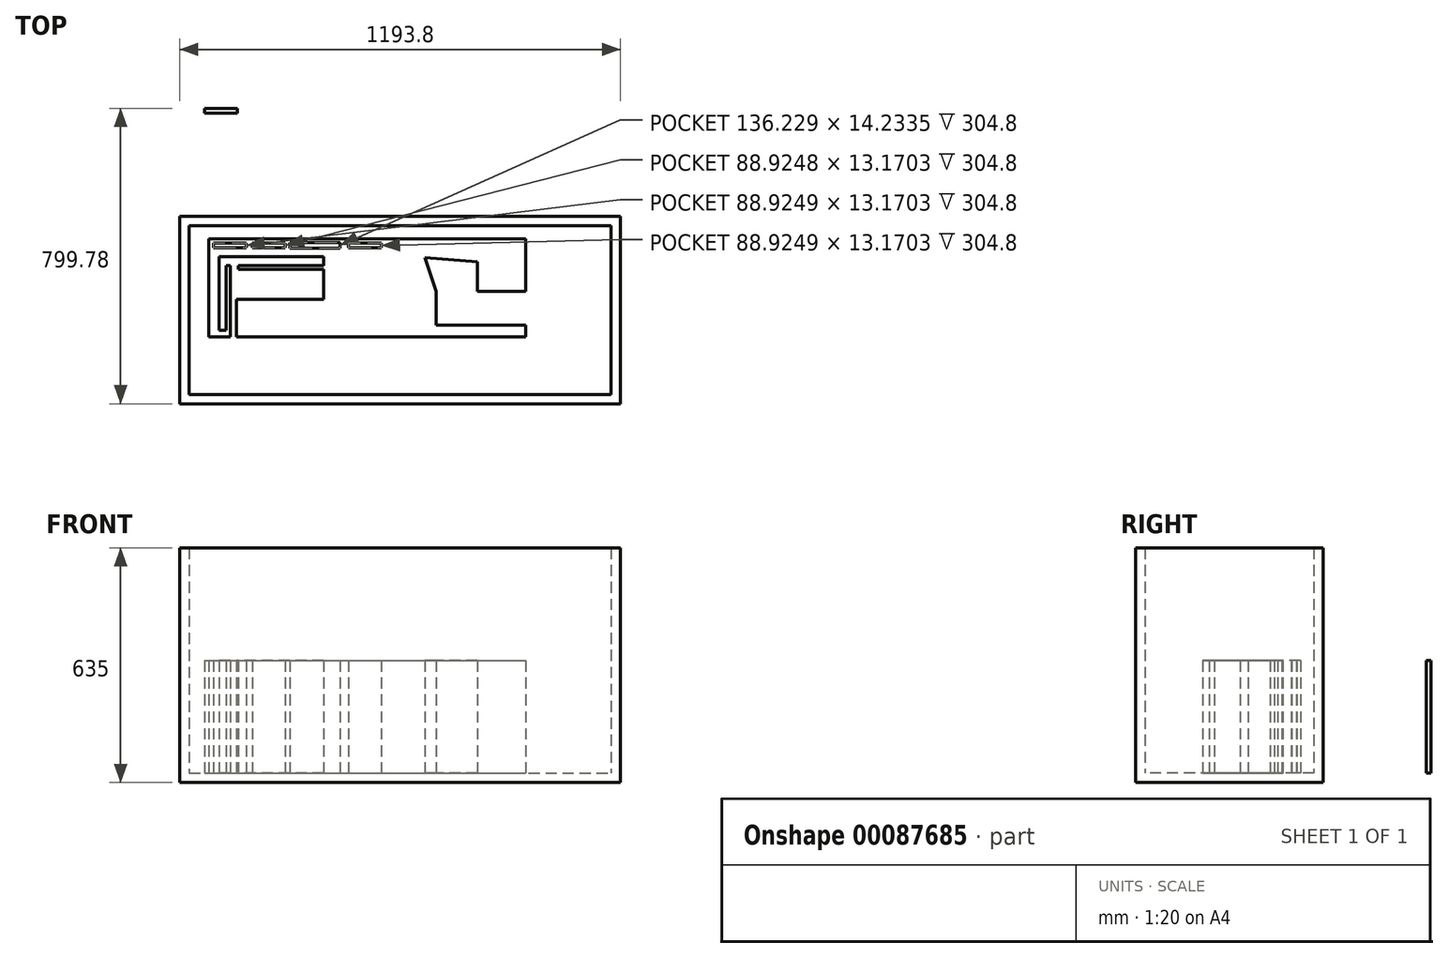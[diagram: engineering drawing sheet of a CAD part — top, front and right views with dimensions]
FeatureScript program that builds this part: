
annotation { "Feature Type Name" : "Feature", "Feature Type Description" : "" }
export const myFeature = defineFeature(function(context is Context, id is Id, definition is map)
    precondition{}
    {
        {
            var Q0;
            Q0=qCreatedBy(makeId("Top.planeOp"),FACE);
            var sketch = newSketch(context, id + "F0", { "sketchPlane" : qUnion([Q0])});
            skLineSegment(sketch, "E0.bottom", {"start": v(-2897.27, -1894.61) * mm, "end": v(-1754.27, -1894.61) * mm});
            skLineSegment(sketch, "E0.top", {"start": v(-2897.27, -2351.81) * mm, "end": v(-1754.27, -2351.81) * mm});
            skLineSegment(sketch, "E0.left", {"start": v(-2897.27, -1894.61) * mm, "end": v(-2897.27, -2351.81) * mm});
            skLineSegment(sketch, "E0.right", {"start": v(-1754.27, -1894.61) * mm, "end": v(-1754.27, -2351.81) * mm});
            skSolve(sketch);
        }
        {
            var Q0;
            Q0=qSketchRegion(id+"F0",true);
            extrude(context, id + "F1", {"entities" : qUnion([Q0]), "depth" : 609.6 * mm});
        }
        {
            var Q0;
            Q0=makeQuery(id+"F1.opExtrude","CAP_FACE",FACE,{"disambiguationData":[OSD([sQuery(id+"F0.wireOp",EDGE,"E0.bottom"),sQuery(id+"F0.wireOp",EDGE,"E0.top"),sQuery(id+"F0.wireOp",EDGE,"E0.left"),sQuery(id+"F0.wireOp",EDGE,"E0.right")])],"isStart":false});
            shell(context, id + "F2", {"entities" : qUnion([Q0]), "thickness" : 25.4 * mm, "oppositeDirection" : true});
        }
        {
            var Q0;
            Q0=makeQuery(id+"F0.imprint","IMPRINT",FACE,{"disambiguationData":[TD([[makeQuery(id+"F0.imprint","IMPRINT",EDGE,{"derivedFrom":sQuery(id+"F0.wireOp",EDGE,"E0.bottom")}),-1.0]])]});
            var sketch = newSketch(context, id + "F3", { "sketchPlane" : qUnion([Q0])});
            skLineSegment(sketch, "E1.bottom", {"start": v(-2844.11, -1930.89) * mm, "end": v(-2361.95, -1930.89) * mm});
            skLineSegment(sketch, "E1.top", {"start": v(-2844.11, -2196.1) * mm, "end": v(-2785.55, -2196.1) * mm});
            skLineSegment(sketch, "E1.left", {"start": v(-2844.11, -1930.89) * mm, "end": v(-2844.11, -2196.1) * mm});
            skLineSegment(sketch, "E1.right", {"start": v(-2361.95, -1930.89) * mm, "end": v(-2361.95, -2196.1) * mm});
            skLineSegment(sketch, "E2", {"start": v(-2361.95, -1930.89) * mm, "end": v(-1985.66, -1930.89) * mm});
            skLineSegment(sketch, "E3", {"start": v(-1985.66, -1930.89) * mm, "end": v(-1985.66, -2072.53) * mm});
            skLineSegment(sketch, "E4", {"start": v(-2227.46, -2072.53) * mm, "end": v(-2227.46, -2163.63) * mm});
            skLineSegment(sketch, "E5", {"start": v(-2227.46, -2163.63) * mm, "end": v(-1985.66, -2163.63) * mm});
            skLineSegment(sketch, "E6", {"start": v(-1985.66, -2163.63) * mm, "end": v(-1985.66, -2196.1) * mm});
            skLineSegment(sketch, "E7", {"start": v(-1985.66, -2196.1) * mm, "end": v(-2361.95, -2196.1) * mm});
            skLineSegment(sketch, "E8", {"start": v(-2361.95, -2196.1) * mm, "end": v(-2361.95, -2196.1) * mm});
            skLineSegment(sketch, "E9", {"start": v(-2227.46, -2072.53) * mm, "end": v(-2258.96, -1980.68) * mm});
            skLineSegment(sketch, "E10", {"start": v(-2116.15, -1992.04) * mm, "end": v(-2258.96, -1980.68) * mm});
            skLineSegment(sketch, "E11", {"start": v(-2116.15, -1992.04) * mm, "end": v(-2116.15, -2072.53) * mm});
            skLineSegment(sketch, "E12", {"start": v(-2116.15, -2072.53) * mm, "end": v(-1985.66, -2072.53) * mm});
            skLineSegment(sketch, "E13.bottom", {"start": v(-2725.45, -1941.36) * mm, "end": v(-2636.52, -1941.36) * mm});
            skLineSegment(sketch, "E13.top", {"start": v(-2725.45, -1954.53) * mm, "end": v(-2636.52, -1954.53) * mm});
            skLineSegment(sketch, "E13.left", {"start": v(-2725.45, -1941.36) * mm, "end": v(-2725.45, -1954.53) * mm});
            skLineSegment(sketch, "E13.right", {"start": v(-2636.52, -1941.36) * mm, "end": v(-2636.52, -1954.53) * mm});
            skLineSegment(sketch, "E14.bottom", {"start": v(-2831.71, -1941.36) * mm, "end": v(-2742.79, -1941.36) * mm});
            skLineSegment(sketch, "E14.top", {"start": v(-2831.71, -1954.53) * mm, "end": v(-2742.79, -1954.53) * mm});
            skLineSegment(sketch, "E14.left", {"start": v(-2831.71, -1941.36) * mm, "end": v(-2831.71, -1954.53) * mm});
            skLineSegment(sketch, "E14.right", {"start": v(-2742.79, -1941.36) * mm, "end": v(-2742.79, -1954.53) * mm});
            skLineSegment(sketch, "E15.bottom", {"start": v(-2855.45, -1577.43) * mm, "end": v(-2766.52, -1577.43) * mm});
            skLineSegment(sketch, "E15.top", {"start": v(-2855.45, -1590.6) * mm, "end": v(-2766.52, -1590.6) * mm});
            skLineSegment(sketch, "E15.left", {"start": v(-2855.45, -1577.43) * mm, "end": v(-2855.45, -1590.6) * mm});
            skLineSegment(sketch, "E15.right", {"start": v(-2766.52, -1577.43) * mm, "end": v(-2766.52, -1590.6) * mm});
            skLineSegment(sketch, "E16.bottom", {"start": v(-2624.35, -1955.36) * mm, "end": v(-2488.12, -1955.36) * mm});
            skLineSegment(sketch, "E16.top", {"start": v(-2624.35, -1941.13) * mm, "end": v(-2488.12, -1941.13) * mm});
            skLineSegment(sketch, "E16.left", {"start": v(-2488.12, -1941.13) * mm, "end": v(-2488.12, -1955.36) * mm});
            skLineSegment(sketch, "E16.right", {"start": v(-2624.35, -1941.13) * mm, "end": v(-2624.35, -1955.36) * mm});
            skLineSegment(sketch, "E17.bottom", {"start": v(-2464.96, -1941.36) * mm, "end": v(-2376.03, -1941.36) * mm});
            skLineSegment(sketch, "E17.top", {"start": v(-2464.96, -1954.53) * mm, "end": v(-2376.03, -1954.53) * mm});
            skLineSegment(sketch, "E17.left", {"start": v(-2464.96, -1941.36) * mm, "end": v(-2464.96, -1954.53) * mm});
            skLineSegment(sketch, "E17.right", {"start": v(-2376.03, -1941.36) * mm, "end": v(-2376.03, -1954.53) * mm});
            skLineSegment(sketch, "E18", {"start": v(-2830.27, -1966.6) * mm, "end": v(-2830.27, -2196.1) * mm});
            skLineSegment(sketch, "E19", {"start": v(-2830.27, -1966.6) * mm, "end": v(-2519.61, -1966.6) * mm});
            skLineSegment(sketch, "E20", {"start": v(-2519.61, -1966.6) * mm, "end": v(-2519.61, -2196.1) * mm});
            skLineSegment(sketch, "E21.trimOffspring", {"start": v(-2519.61, -2196.1) * mm, "end": v(-2361.95, -2196.1) * mm});
            skLineSegment(sketch, "E22", {"start": v(-2785.55, -2196.1) * mm, "end": v(-2785.55, -2002.14) * mm});
            skLineSegment(sketch, "E23", {"start": v(-2785.55, -2002.14) * mm, "end": v(-2796.33, -2002.14) * mm});
            skLineSegment(sketch, "E24", {"start": v(-2796.33, -2002.14) * mm, "end": v(-2796.33, -2177.75) * mm});
            skLineSegment(sketch, "E25", {"start": v(-2796.33, -2177.75) * mm, "end": v(-2816.27, -2177.75) * mm});
            skLineSegment(sketch, "E26", {"start": v(-2816.27, -2177.75) * mm, "end": v(-2816.27, -1978.45) * mm});
            skLineSegment(sketch, "E27", {"start": v(-2816.27, -1978.45) * mm, "end": v(-2532.95, -1978.45) * mm});
            skLineSegment(sketch, "E28", {"start": v(-2532.95, -1978.45) * mm, "end": v(-2532.95, -2002.14) * mm});
            skLineSegment(sketch, "E29", {"start": v(-2532.95, -2002.14) * mm, "end": v(-2764.51, -2002.14) * mm});
            skLineSegment(sketch, "E30", {"start": v(-2764.51, -2002.14) * mm, "end": v(-2764.51, -2013.48) * mm});
            skLineSegment(sketch, "E31", {"start": v(-2764.51, -2013.48) * mm, "end": v(-2532.81, -2013.48) * mm});
            skLineSegment(sketch, "E32", {"start": v(-2532.81, -2013.48) * mm, "end": v(-2532.81, -2094.28) * mm});
            skLineSegment(sketch, "E33", {"start": v(-2532.81, -2094.28) * mm, "end": v(-2768.37, -2094.28) * mm});
            skLineSegment(sketch, "E34", {"start": v(-2768.37, -2094.28) * mm, "end": v(-2768.37, -2196.1) * mm});
            skLineSegment(sketch, "E35", {"start": v(-2768.37, -2196.1) * mm, "end": v(-2708.45, -2196.1) * mm});
            skLineSegment(sketch, "E36", {"start": v(-2708.45, -2196.1) * mm, "end": v(-2519.61, -2196.1) * mm});
            skSolve(sketch);
        }
        {
            var Q0;
            Q0 = qSketchRegion(id + "F3", true);
            extrude(context, id + "F4", {"entities" : qUnion([Q0]), "operationType" : NewBodyOperationType.ADD, "depth" : 304.8 * mm, "offsetDistance" : 30.48 * mm});
        }
    });
